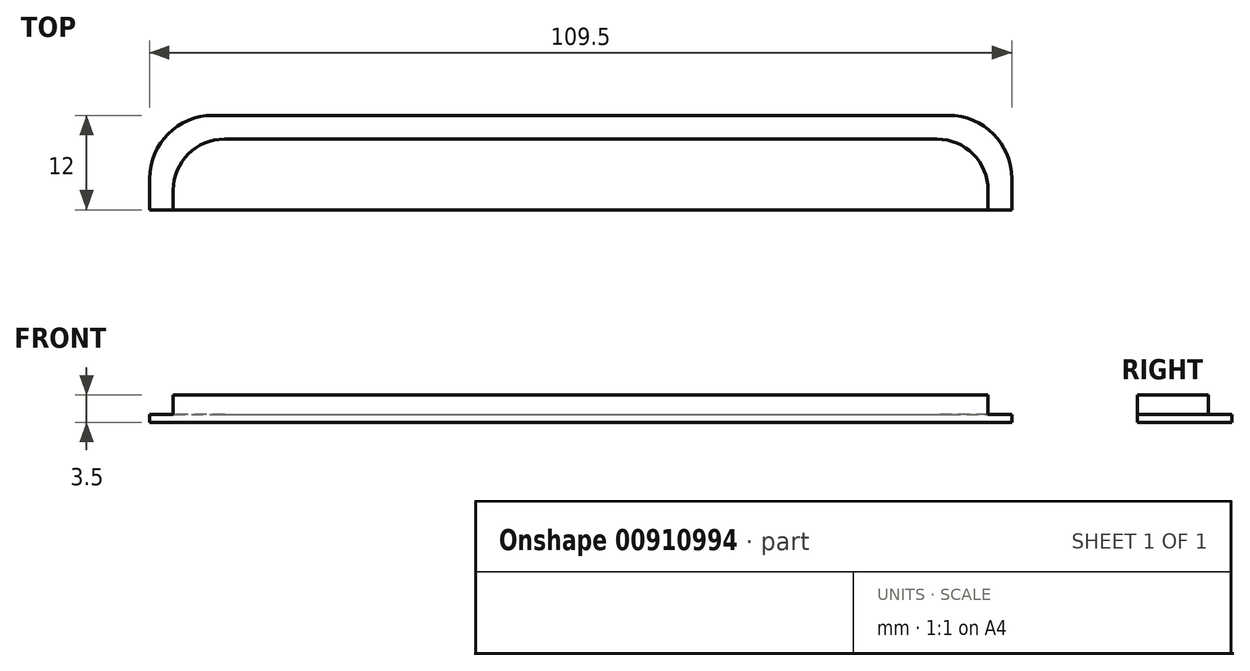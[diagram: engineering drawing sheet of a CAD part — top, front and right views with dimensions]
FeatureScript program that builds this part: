
annotation { "Feature Type Name" : "Feature", "Feature Type Description" : "" }
export const myFeature = defineFeature(function(context is Context, id is Id, definition is map)
    precondition{}
    {
        {
            var Q0;
            Q0=qCreatedBy(makeId("Top.planeOp"),FACE);
            var sketch = newSketch(context, id + "F0", { "sketchPlane" : qUnion([Q0])});
            skLineSegment(sketch, "E0.bottom", {"start": v(0, 0) * mm, "end": v(103.5, 0) * mm});
            skLineSegment(sketch, "E0.top", {"start": v(0, -9) * mm, "end": v(103.5, -9) * mm});
            skLineSegment(sketch, "E0.left", {"start": v(0, 0) * mm, "end": v(0, -9) * mm});
            skLineSegment(sketch, "E0.right", {"start": v(103.5, 0) * mm, "end": v(103.5, -9) * mm});
            skSolve(sketch);
        }
        {
            var Q0;
            Q0 = qSketchRegion(id + "F0", true);
            extrude(context, id + "F1", {"entities" : qUnion([Q0]), "depth" : 2.5 * mm, "offsetDistance" : 25 * mm});
        }
        {
            var Q0;
            Q0=makeQuery(id+"F1.opExtrude","SWEPT_EDGE",EDGE,{"disambiguationData":[OSD([sQuery(id+"F0.wireOp",EDGE,"E0.bottom"),sQuery(id+"F0.wireOp",EDGE,"E0.right")])]});
            var Q1;
            Q1=makeQuery(id+"F1.opExtrude","SWEPT_EDGE",EDGE,{"disambiguationData":[OSD([sQuery(id+"F0.wireOp",EDGE,"E0.bottom"),sQuery(id+"F0.wireOp",EDGE,"E0.left")])]});
            fillet(context, id + "F2", {"entities" : qUnion([Q0, Q1]), "radius" : 6.5 * mm, "tangentPropagation" : true, "allowEdgeOverflow" : false});
        }
        {
            var Q0;
            Q0=makeQuery(id+"F1.opExtrude","CAP_FACE",FACE,{"disambiguationData":[OSD([sQuery(id+"F0.wireOp",EDGE,"E0.bottom"),sQuery(id+"F0.wireOp",EDGE,"E0.top"),sQuery(id+"F0.wireOp",EDGE,"E0.left"),sQuery(id+"F0.wireOp",EDGE,"E0.right")])],"isStart":true});
            var sketch = newSketch(context, id + "F3", { "sketchPlane" : qUnion([Q0])});
            skLineSegment(sketch, "E1.bottom", {"start": v(-3, 9) * mm, "end": v(106.5, 9) * mm});
            skLineSegment(sketch, "E1.top", {"start": v(-3, -3) * mm, "end": v(106.5, -3) * mm});
            skLineSegment(sketch, "E1.left", {"start": v(-3, 9) * mm, "end": v(-3, -3) * mm});
            skLineSegment(sketch, "E1.right", {"start": v(106.5, 9) * mm, "end": v(106.5, -3) * mm});
            skSolve(sketch);
        }
        {
            var Q0;
            Q0 = qSketchRegion(id + "F3", true);
            extrude(context, id + "F4", {"entities" : qUnion([Q0]), "operationType" : NewBodyOperationType.ADD, "depth" : 1 * mm, "offsetDistance" : 25 * mm});
        }
        {
            var Q0;
            Q0=makeQuery(id+"F4.opExtrude","SWEPT_EDGE",EDGE,{"disambiguationData":[OSD([sQuery(id+"F3.wireOp",EDGE,"E1.top"),sQuery(id+"F3.wireOp",EDGE,"E1.right")])]});
            var Q1;
            Q1=makeQuery(id+"F4.opExtrude","SWEPT_EDGE",EDGE,{"disambiguationData":[OSD([sQuery(id+"F3.wireOp",EDGE,"E1.top"),sQuery(id+"F3.wireOp",EDGE,"E1.left")])]});
            fillet(context, id + "F5", {"entities" : qUnion([Q0, Q1]), "radius" : 8 * mm, "tangentPropagation" : true, "allowEdgeOverflow" : false});
        }
    });
